# Revit family: Shower-Showerhead_Kit-KALLISTA-For_Town-P21542
name_source: partatom
category: Plumbing Fixtures
units: mm (PartAtom-declared; Revit-internal decimal feet)

## family parameters
Cut with Voids When Loaded = No
Host = Face
Maintain Annotation Orientation = No
OmniClass Number = 23.31.17.00
OmniClass Title = Showers
Part Type = Normal
Room Calculation Point = No
Round Connector Dimension = Use Diameter
Shared = No

## types (2) — shared parameters
ADA Compliant = No
Assembly Code = D2010700
CW Connection = No
Cold Water Inlet = Cold Water Inlet
Date Modified = 05/07/2025
Default Elevation = 72"
Description = Traditional Multi-Function Handshower with Hose
Drain Included = No
Flow Rate = 2 GPM
HW Connection = Yes
Height = 9 9/16"
Hot Water Inlet = Hot Water Inlet
Length = 6 13/16"
Manufacturer = Kallista Co.
Master Format 2014 = 22 42 23
Master Format 2014 Name = Residential Showers
Material = Premium Metal Construction
Pressure = 80.00 psi
Product Documentation Link = https://techcomm.kohler.com
Product Name = For Town
Product Page URL = https://www.kallista.com
Tempered Water Inlet = Tempered Water Inlet
URL = https://www.kallista.com
Vent Connection = No
Waste Connection = No
Waste Water Outlet = Waste Water Outlet
WaterSense Certified = No
Width = 4 11/16"

## per-type parameters (varying)
| type | Finish | Model | Type |
| AD-Nickel Silver | Kallista-Metal-AD-Nickel_Silver | P21542-00-AD | 1 |
| CP-Chrome | Kallista-Metal-CP-Chrome | P21542-00-CP | 2 |

## geometry (parser evidence)
native form markers: Sweep x6
no freeform markers — native parametric forms only
